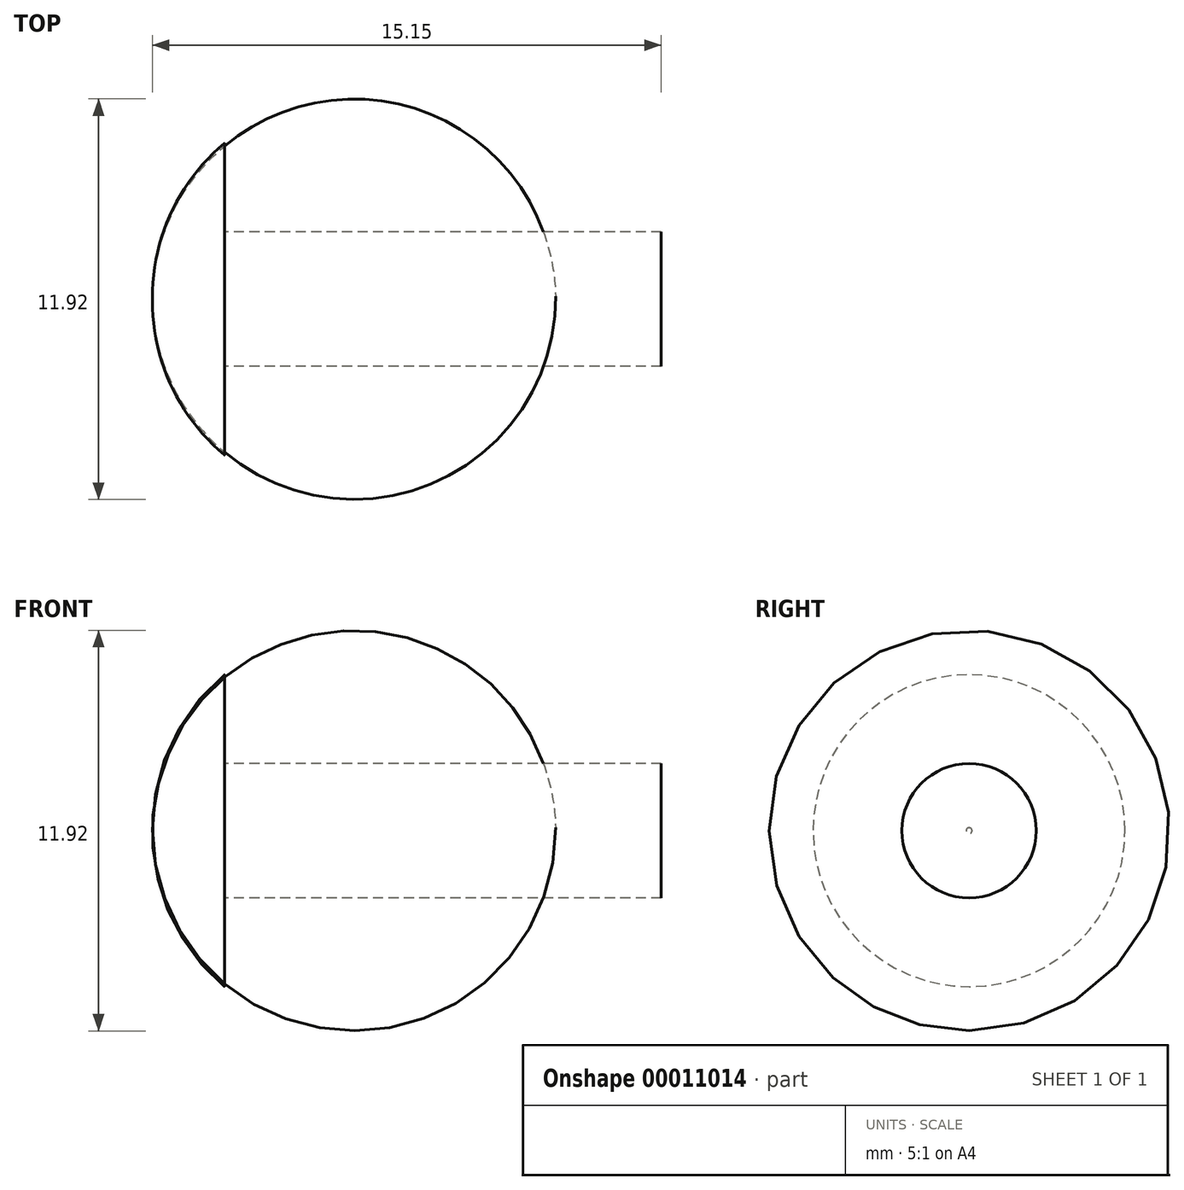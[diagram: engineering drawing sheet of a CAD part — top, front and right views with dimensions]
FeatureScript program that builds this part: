
annotation { "Feature Type Name" : "Feature", "Feature Type Description" : "" }
export const myFeature = defineFeature(function(context is Context, id is Id, definition is map)
    precondition{}
    {
        {
            var Q0;
            Q0=qCreatedBy(makeId("Front.planeOp"),FACE);
            var sketch = newSketch(context, id + "F0", { "sketchPlane" : qUnion([Q0])});
            skLineSegment(sketch, "E0", {"start": v(-14.1, 0) * mm, "end": v(28.18, 0) * mm, "construction": true});
            skLineSegment(sketch, "E1", {"start": v(13, 0) * mm, "end": v(13, 2) * mm});
            skLineSegment(sketch, "E2", {"start": v(13, 2) * mm, "end": v(0, 2) * mm});
            skLineSegment(sketch, "E3", {"start": v(0, 2) * mm, "end": v(0, 4.64) * mm});
            skArc(sketch, "E4", {"start": v(0, 4.64) * mm, "mid": v(-1.6, 2.56) * mm, "end": v(-2.15, 0) * mm});
            skLineSegment(sketch, "E5", {"start": v(-2.15, 0) * mm, "end": v(13, 0) * mm});
            skSolve(sketch);
        }
        {
            var Q0;
            Q0 = qSketchRegion(id + "F0", true);
            var Q1;
            Q1=sQuery(id+"F0.wireOp",EDGE,"E0");
            revolve(context, id + "F1", {"entities" : qUnion([Q0]), "axis" : qUnion([Q1]), "revolveType" : RevolveType.FULL});
        }
    });
